# Revit family: AV4090001_Aluvia Teleducha
name_source: partatom
category: Plumbing Fixtures
units: mm (PartAtom-declared; Revit-internal decimal feet)

## family parameters
Always vertical = Yes
Cut with Voids When Loaded = No
OmniClass Number = 23.31.11.00
OmniClass Title = Faucets
Part Type = Normal
Room Calculation Point = No
Round Connector Dimension = Use Diameter
Shared = No
Work Plane-Based = No

## types (1)
- AV4090001_Aluvia Teleducha
    Acabado = Cromado
    Alto = 243 mm  [stored 0.797244 ft]
    Ancho = 101 mm  [stored 0.331365 ft]
    Capacidad de flujo = a 80 psi: 9,3 L/min
    Creado por = BIMBAU
    Default Elevation = 0 mm  [stored 0 ft]
    Description = La teleducha Aluvia con tamaño medio y chorro tipo lluvia focalizado ofrece mayor practicidad, ideal para consumidores que buscan cobertura direccionada.
    Fecha de creación = 16/03/2021
    Garantía = 30 Años
    Manufacturer = Corona
    Material = Ceilings
    Material 2 = Corona_Plastico_Gris
    Model = Aluvia Teleducha
    Peso neto = 400 g. - 1,03 lb.
    Presion maxima = 125 psi (860 kPa).
    Presion minima = 20 psi (140 kPa).
    Profundidad = 48 mm  [stored 0.15748 ft]
    Referencia = AV4090001
    Temperatura de Uso = 5˚C a 71˚C.

note: [stored X ft] marks values corroborated as IEEE doubles in the binary element streams (Revit-internal decimal feet)

## geometry (parser evidence)
native form markers: Sweep x3
no freeform markers — native parametric forms only
